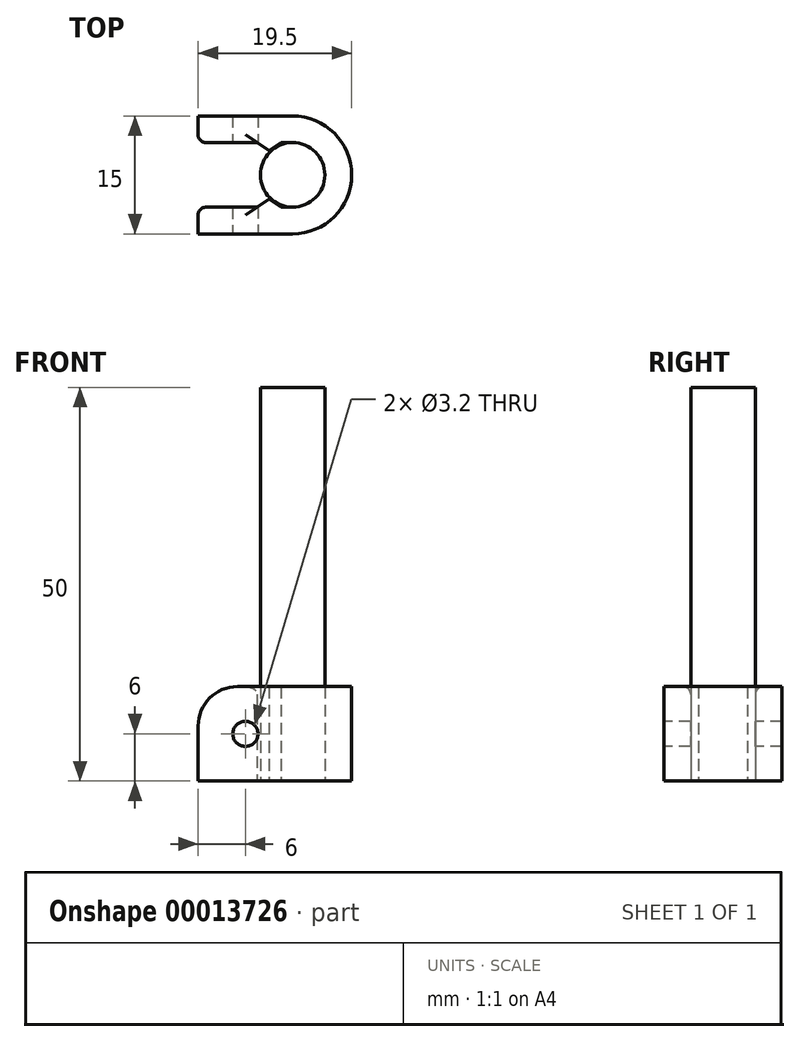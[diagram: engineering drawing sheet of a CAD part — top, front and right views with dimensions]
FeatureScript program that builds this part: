
annotation { "Feature Type Name" : "Feature", "Feature Type Description" : "" }
export const myFeature = defineFeature(function(context is Context, id is Id, definition is map)
    precondition{}
    {
        {
            var Q0;
            Q0=qCreatedBy(makeId("Top.planeOp"),FACE);
            var sketch = newSketch(context, id + "F0", { "sketchPlane" : qUnion([Q0])});
            skCircle(sketch, "E0", {"center": v(0, 0) * mm, "radius": 4.1 * mm});
            skArc(sketch, "E1", {"start": v(0, -7.5) * mm, "mid": v(7.5, 0) * mm, "end": v(0, 7.5) * mm});
            skLineSegment(sketch, "E2", {"start": v(0, -7.5) * mm, "end": v(-12, -7.5) * mm});
            skLineSegment(sketch, "E3", {"start": v(0, 7.5) * mm, "end": v(-12, 7.5) * mm});
            skLineSegment(sketch, "E4", {"start": v(-12, -7.5) * mm, "end": v(-12, -4.1) * mm});
            skLineSegment(sketch, "E5", {"start": v(0, 4.1) * mm, "end": v(-1.5, 4.1) * mm});
            skLineSegment(sketch, "E6", {"start": v(0, -4.1) * mm, "end": v(-1.5, -4.1) * mm});
            skLineSegment(sketch, "E7.trimOffspring", {"start": v(-12, 4.1) * mm, "end": v(-12, 7.5) * mm});
            skLineSegment(sketch, "E8", {"start": v(-6.5, -7.5) * mm, "end": v(-6.5, 7.5) * mm, "construction": true});
            skLineSegment(sketch, "E9", {"start": v(-4.9, -7.5) * mm, "end": v(-4.9, 7.5) * mm, "construction": true});
            skLineSegment(sketch, "E10", {"start": v(-8.1, 7.5) * mm, "end": v(-8.1, -7.5) * mm, "construction": true});
            skLineSegment(sketch, "E11", {"start": v(-6.5, 6.2) * mm, "end": v(-8.1, 6.2) * mm, "construction": true});
            skLineSegment(sketch, "E12", {"start": v(-6.5, 6.2) * mm, "end": v(-4.9, 6.2) * mm, "construction": true});
            skLineSegment(sketch, "E13", {"start": v(-4.5, 4.1) * mm, "end": v(-3, 3.1) * mm});
            skLineSegment(sketch, "E14", {"start": v(-3, 3.1) * mm, "end": v(-1.5, 4.1) * mm});
            skLineSegment(sketch, "E15", {"start": v(-1.5, -4.1) * mm, "end": v(-3, -3.1) * mm});
            skLineSegment(sketch, "E16", {"start": v(-3, -3.1) * mm, "end": v(-4.5, -4.1) * mm});
            skLineSegment(sketch, "E17", {"start": v(-3, -3.1) * mm, "end": v(-3, -4.1) * mm, "construction": true});
            skLineSegment(sketch, "E18", {"start": v(-3, 3.1) * mm, "end": v(-3, 4.1) * mm, "construction": true});
            skLineSegment(sketch, "E19.trimOffspring", {"start": v(-4.5, -4.1) * mm, "end": v(-12, -4.1) * mm});
            skLineSegment(sketch, "E20.trimOffspring", {"start": v(-4.5, 4.1) * mm, "end": v(-12, 4.1) * mm});
            skLineSegment(sketch, "E21", {"start": v(-12, -7.5) * mm, "end": v(-12, -15.5) * mm});
            skLineSegment(sketch, "E22", {"start": v(-12, -15.5) * mm, "end": v(-4, -15.5) * mm});
            skLineSegment(sketch, "E23", {"start": v(-4, -15.5) * mm, "end": v(-4, -7.5) * mm});
            skLineSegment(sketch, "E24", {"start": v(-12, 7.5) * mm, "end": v(-12, 15.5) * mm});
            skLineSegment(sketch, "E25", {"start": v(-12, 15.5) * mm, "end": v(-4, 15.5) * mm});
            skLineSegment(sketch, "E26", {"start": v(-4, 15.5) * mm, "end": v(-4, 7.5) * mm});
            skCircle(sketch, "E27", {"center": v(-8, -11.5) * mm, "radius": 1.6 * mm});
            skCircle(sketch, "E28", {"center": v(-8, 11.5) * mm, "radius": 1.6 * mm});
            skLineSegment(sketch, "E29", {"start": v(-8, 15.5) * mm, "end": v(-8, 11.5) * mm, "construction": true});
            skLineSegment(sketch, "E30", {"start": v(-12, 11.5) * mm, "end": v(-8, 11.5) * mm, "construction": true});
            skLineSegment(sketch, "E31", {"start": v(-8, -15.5) * mm, "end": v(-8, -11.5) * mm, "construction": true});
            skLineSegment(sketch, "E32", {"start": v(-12, -11.5) * mm, "end": v(-8, -11.5) * mm, "construction": true});
            skSolve(sketch);
        }
        {
            var Q0;
            Q0=makeQuery(id+"F0.imprint","IMPRINT",FACE,{"disambiguationData":[TD([[makeQuery(id+"F0.imprint","IMPRINT",EDGE,{"derivedFrom":sQuery(id+"F0.wireOp",EDGE,"E1")}),1.0]])]});
            extrude(context, id + "F1", {"entities" : qUnion([Q0]), "depth" : 12 * mm});
        }
        {
            var Q0;
            Q0=makeQuery(id+"F1.opExtrude","SWEPT_FACE",FACE,{"disambiguationData":[OSD([sQuery(id+"F0.wireOp",EDGE,"E2")])]});
            var sketch = newSketch(context, id + "F2", { "sketchPlane" : qUnion([Q0])});
            skCircle(sketch, "E33", {"center": v(-6, 6) * mm, "radius": 1.6 * mm});
            skSolve(sketch);
        }
        {
            var Q0;
            {var subQ0=sQuery(id+"F0.wireOp",EDGE,"E0");var subQ2=makeQuery(id+"F0.imprint","INTERSECT",VERTEX,{"derivedFrom":[subQ0,sQuery(id+"F0.wireOp",EDGE,"E5")]});Q0=makeQuery(id+"F0.imprint","IMPRINT",FACE,{"disambiguationData":[TD([[makeQuery(id+"F0.imprint","IMPRINT",EDGE,{"disambiguationData":[TD([[subQ2,-1.0]])],"derivedFrom":subQ0}),1.0]])]});}
            extrude(context, id + "F3", {"entities" : qUnion([Q0]), "depth" : 50 * mm});
        }
        {
            var Q0;
            Q0=makeQuery(id+"F2.imprint","IMPRINT",FACE,{"disambiguationData":[TD([[makeQuery(id+"F2.imprint","IMPRINT",EDGE,{"derivedFrom":sQuery(id+"F2.wireOp",EDGE,"E33")}),1.0]])]});
            extrude(context, id + "F4", {"entities" : qUnion([Q0]), "operationType" : NewBodyOperationType.REMOVE, "endBound" : BoundingType.THROUGH_ALL, "oppositeDirection" : true, "depth" : 15.63 * mm});
        }
        {
            var Q0;
            Q0=makeQuery(id+"F1.opExtrude","CAP_EDGE",EDGE,{"disambiguationData":[OSD([sQuery(id+"F0.wireOp",EDGE,"E4")])],"isStart":false});
            var Q1;
            Q1=makeQuery(id+"F1.opExtrude","CAP_EDGE",EDGE,{"disambiguationData":[OSD([sQuery(id+"F0.wireOp",EDGE,"E7.trimOffspring")])],"isStart":false});
            fillet(context, id + "F5", {"entities" : qUnion([Q0, Q1]), "radius" : 5 * mm, "tangentPropagation" : true, "allowEdgeOverflow" : false});
        }
        {
            var Q0;
            Q0=makeQuery(id+"F1.opExtrude","SWEPT_EDGE",EDGE,{"disambiguationData":[OSD([sQuery(id+"F0.wireOp",EDGE,"E7.trimOffspring"),sQuery(id+"F0.wireOp",EDGE,"E20.trimOffspring")])]});
            var Q1;
            Q1=makeQuery(id+"F1.opExtrude","SWEPT_EDGE",EDGE,{"disambiguationData":[OSD([sQuery(id+"F0.wireOp",EDGE,"E4"),sQuery(id+"F0.wireOp",EDGE,"E19.trimOffspring")])]});
            fillet(context, id + "F6", {"entities" : qUnion([Q0, Q1]), "radius" : 1 * mm, "tangentPropagation" : true, "allowEdgeOverflow" : false});
        }
    });
